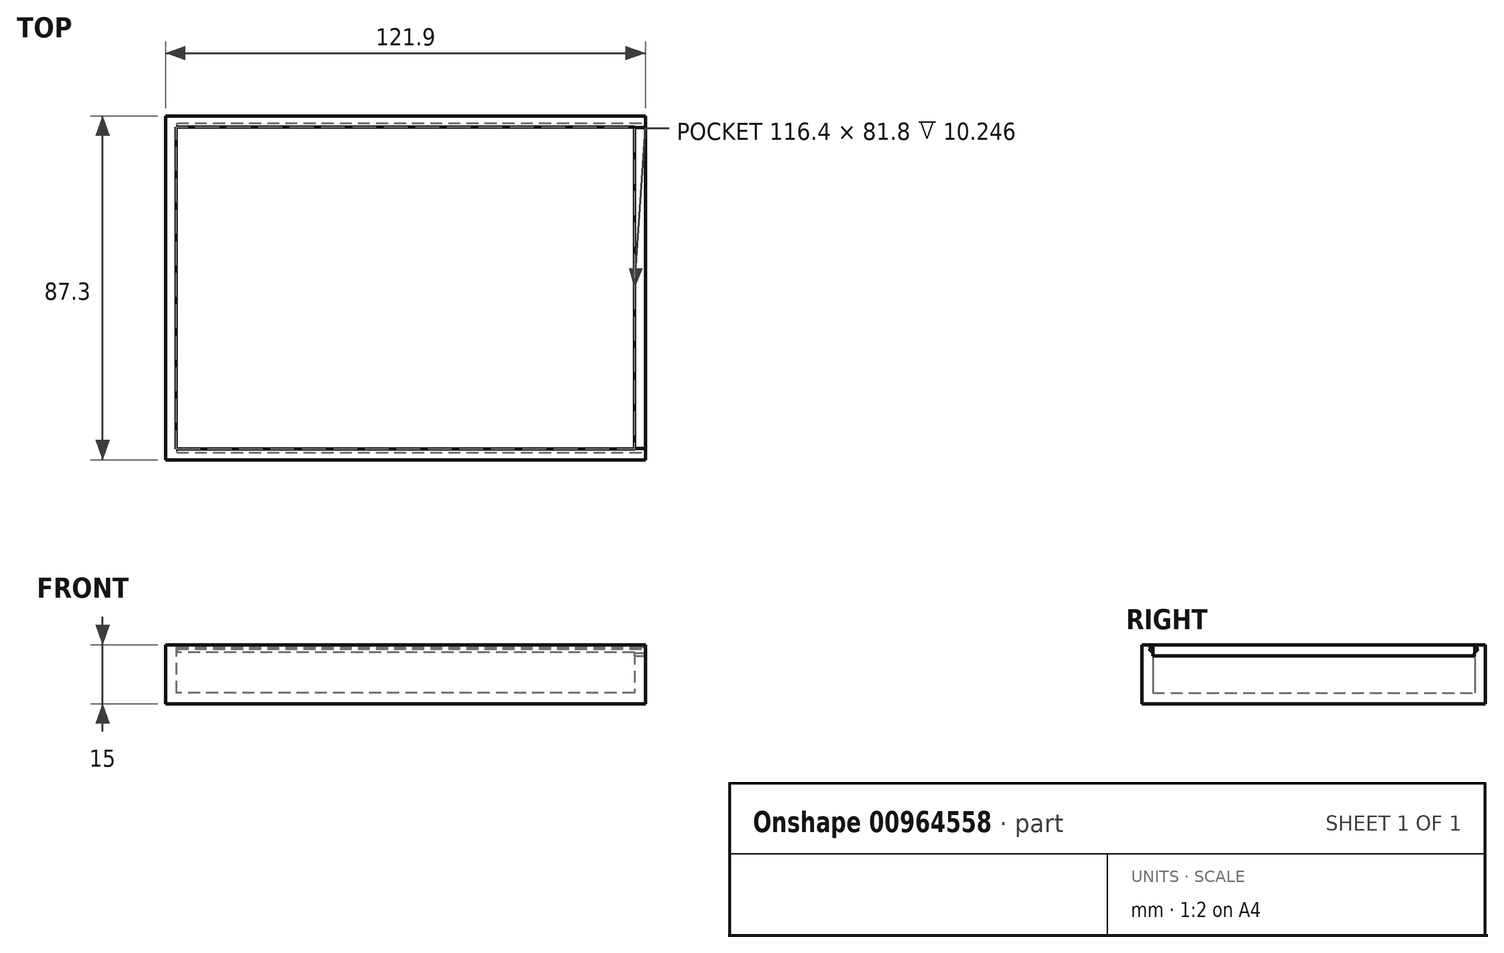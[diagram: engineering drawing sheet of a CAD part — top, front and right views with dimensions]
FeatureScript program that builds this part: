
annotation { "Feature Type Name" : "Feature", "Feature Type Description" : "" }
export const myFeature = defineFeature(function(context is Context, id is Id, definition is map)
    precondition{}
    {
        {
            var Q0;
            Q0=qCreatedBy(makeId("Top.planeOp"),FACE);
            var sketch = newSketch(context, id + "F0", { "sketchPlane" : qUnion([Q0])});
            skLineSegment(sketch, "E0.bottom", {"start": v(54.45, -38.15) * mm, "end": v(-54.45, -38.15) * mm});
            skLineSegment(sketch, "E0.top", {"start": v(54.45, 38.15) * mm, "end": v(-54.45, 38.15) * mm});
            skLineSegment(sketch, "E0.left", {"start": v(54.45, -38.15) * mm, "end": v(54.45, 38.15) * mm});
            skLineSegment(sketch, "E0.right", {"start": v(-54.45, -38.15) * mm, "end": v(-54.45, 38.15) * mm});
            skPoint(sketch, "E0.middle", {"position": v(0, 0) * mm});
            skSolve(sketch);
        }
        {
            var Q0;
            Q0 = qSketchRegion(id + "F0", true);
            extrude(context, id + "F1", {"entities" : qUnion([Q0]), "depth" : 15 * mm, "offsetDistance" : 25 * mm});
        }
        {
            var Q0;
            Q0=qCreatedBy(makeId("Top.planeOp"),FACE);
            var sketch = newSketch(context, id + "F2", { "sketchPlane" : qUnion([Q0])});
            skLineSegment(sketch, "E1.bottom", {"start": v(60.95, -43.65) * mm, "end": v(-60.95, -43.65) * mm});
            skLineSegment(sketch, "E1.top", {"start": v(60.95, 43.65) * mm, "end": v(-60.95, 43.65) * mm});
            skLineSegment(sketch, "E1.left", {"start": v(60.95, -43.65) * mm, "end": v(60.95, 43.65) * mm});
            skLineSegment(sketch, "E1.right", {"start": v(-60.95, -43.65) * mm, "end": v(-60.95, 43.65) * mm});
            skPoint(sketch, "E1.middle", {"position": v(0, 0) * mm});
            skSolve(sketch);
        }
        {
            var Q0;
            Q0 = qSketchRegion(id + "F2", true);
            extrude(context, id + "F3", {"entities" : qUnion([Q0]), "operationType" : NewBodyOperationType.ADD, "depth" : 15 * mm, "offsetDistance" : 25 * mm});
        }
        {
            var Q0;
            Q0=makeQuery(id+"F3.opExtrude","CAP_FACE",FACE,{"disambiguationData":[OSD([sQuery(id+"F2.wireOp",EDGE,"E1.bottom"),sQuery(id+"F2.wireOp",EDGE,"E1.top"),sQuery(id+"F2.wireOp",EDGE,"E1.left"),sQuery(id+"F2.wireOp",EDGE,"E1.right")])],"isStart":false});
            shell(context, id + "F4", {"entities" : qUnion([Q0]), "thickness" : 2.75 * mm});
        }
        {
            var Q0;
            Q0=makeQuery(id+"F3.opExtrude","SWEPT_EDGE",EDGE,{"disambiguationData":[OSD([sQuery(id+"F2.wireOp",EDGE,"E1.bottom"),sQuery(id+"F2.wireOp",EDGE,"E1.left")])]});
            cPlane(context, id + "F5", {"entities" : qUnion([Q0]), "cplaneType" : CPlaneType.LINE_ANGLE, "offset" : 25 * mm, "angle" : 0 * degree, "width" : 150 * mm, "height" : 150 * mm});
        }
        {
            var Q0;
            Q0=qCreatedBy(id+"F5.planeOp",FACE);
            var sketch = newSketch(context, id + "F6", { "sketchPlane" : qUnion([Q0])});
            skLineSegment(sketch, "E2", {"start": v(40.8, 15) * mm, "end": v(40.8, 14.5) * mm});
            skLineSegment(sketch, "E3", {"start": v(40.8, 14.5) * mm, "end": v(41.83, 13.88) * mm});
            skLineSegment(sketch, "E4", {"start": v(41.83, 13.88) * mm, "end": v(40.8, 12.9) * mm});
            skLineSegment(sketch, "E5", {"start": v(40.8, 12.9) * mm, "end": v(40.8, 12.2) * mm});
            skLineSegment(sketch, "E6.MirrorCS", {"start": v(-40.8, 15) * mm, "end": v(-40.8, 14.5) * mm});
            skLineSegment(sketch, "E7.MirrorCS", {"start": v(-40.8, 14.5) * mm, "end": v(-41.83, 13.88) * mm});
            skLineSegment(sketch, "E8.MirrorCS", {"start": v(-41.83, 13.88) * mm, "end": v(-40.8, 12.9) * mm});
            skLineSegment(sketch, "E9.MirrorCS", {"start": v(-40.8, 12.9) * mm, "end": v(-40.8, 12.2) * mm});
            skLineSegment(sketch, "E10", {"start": v(40.8, 15) * mm, "end": v(-40.8, 15) * mm});
            skLineSegment(sketch, "E11", {"start": v(-40.8, 12.2) * mm, "end": v(40.8, 12.2) * mm});
            skSolve(sketch);
        }
        {
            var Q0;
            Q0 = qSketchRegion(id + "F6", true);
            extrude(context, id + "F7", {"entities" : qUnion([Q0]), "operationType" : NewBodyOperationType.REMOVE, "depth" : 119 * mm, "offsetDistance" : 25 * mm});
        }
    });
